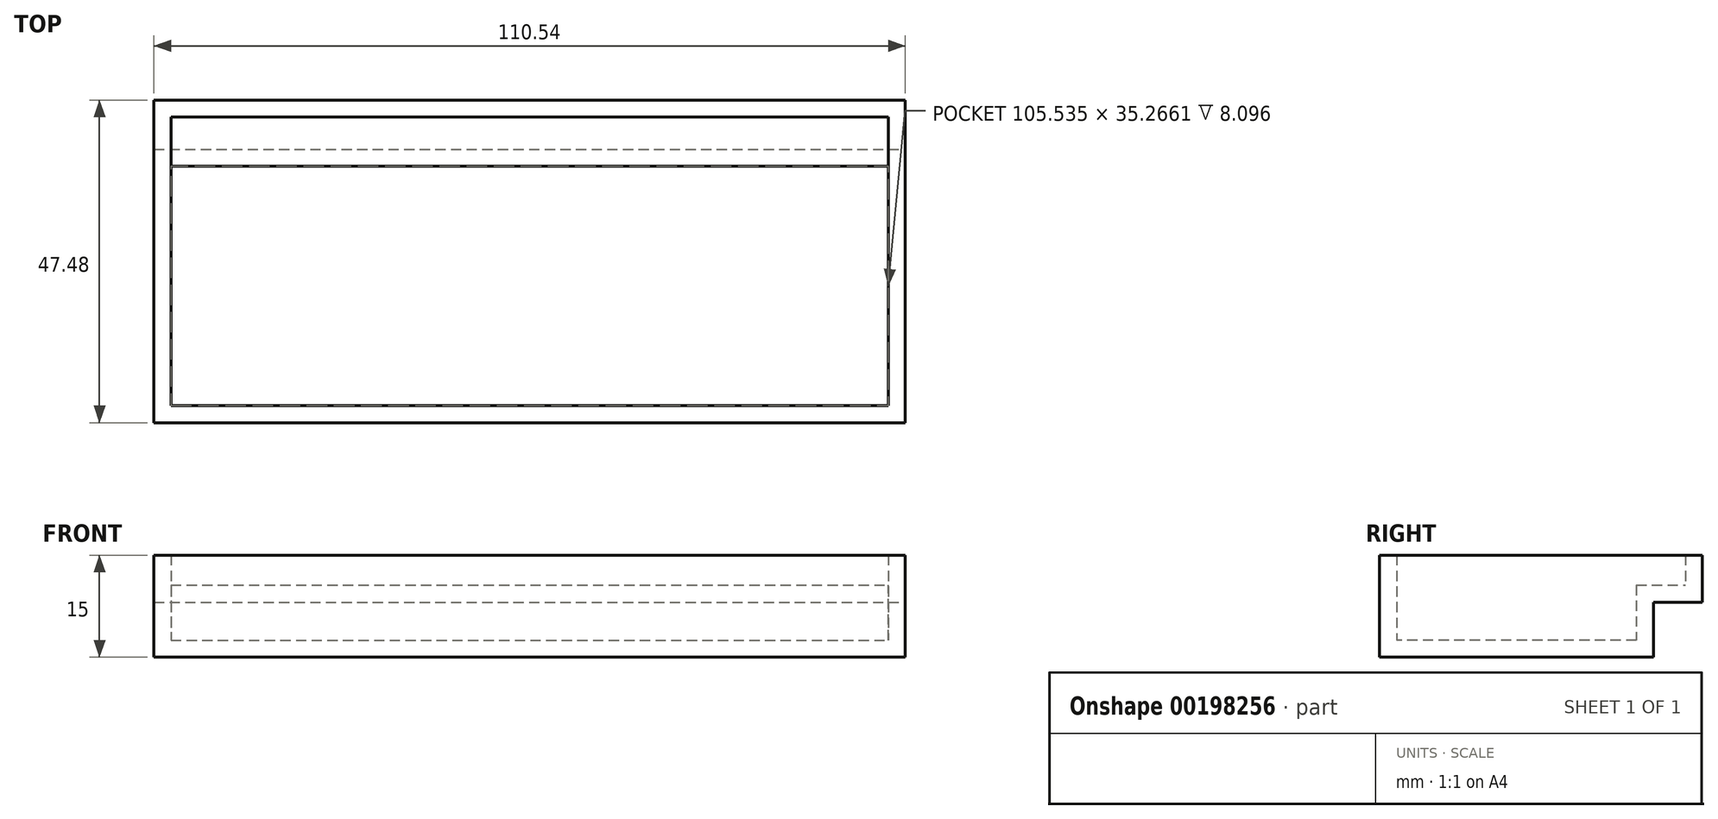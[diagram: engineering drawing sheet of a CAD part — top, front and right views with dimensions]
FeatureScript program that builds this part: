
annotation { "Feature Type Name" : "Feature", "Feature Type Description" : "" }
export const myFeature = defineFeature(function(context is Context, id is Id, definition is map)
    precondition{}
    {
        {
            var Q0;
            Q0=qCreatedBy(makeId("Top.planeOp"),FACE);
            var sketch = newSketch(context, id + "F0", { "sketchPlane" : qUnion([Q0])});
            skLineSegment(sketch, "E0.bottom", {"start": v(-55.88, 22.7) * mm, "end": v(54.66, 22.7) * mm});
            skLineSegment(sketch, "E0.top", {"start": v(-55.88, -24.79) * mm, "end": v(54.66, -24.79) * mm});
            skLineSegment(sketch, "E0.left", {"start": v(-55.88, 22.7) * mm, "end": v(-55.88, -24.79) * mm});
            skLineSegment(sketch, "E0.right", {"start": v(54.66, 22.7) * mm, "end": v(54.66, -24.79) * mm});
            skSolve(sketch);
        }
        {
            var Q0;
            Q0 = qSketchRegion(id + "F0", true);
            extrude(context, id + "F1", {"entities" : qUnion([Q0]), "depth" : 15 * mm});
        }
        {
            var Q0;
            Q0=makeQuery(id+"F1.opExtrude","SWEPT_FACE",FACE,{"disambiguationData":[OSD([sQuery(id+"F0.wireOp",EDGE,"E0.right")])]});
            var sketch = newSketch(context, id + "F2", { "sketchPlane" : qUnion([Q0])});
            skLineSegment(sketch, "E1.bottom", {"start": v(22.7, 0) * mm, "end": v(15.48, 0) * mm});
            skLineSegment(sketch, "E1.top", {"start": v(22.7, 8.1) * mm, "end": v(15.48, 8.1) * mm});
            skLineSegment(sketch, "E1.left", {"start": v(22.7, 0) * mm, "end": v(22.7, 8.1) * mm});
            skLineSegment(sketch, "E1.right", {"start": v(15.48, 0) * mm, "end": v(15.48, 8.1) * mm});
            skSolve(sketch);
        }
        {
            var Q0;
            Q0 = qSketchRegion(id + "F2", true);
            extrude(context, id + "F3", {"entities" : qUnion([Q0]), "operationType" : NewBodyOperationType.REMOVE, "endBound" : BoundingType.UP_TO_NEXT, "oppositeDirection" : true, "depth" : 25 * mm});
        }
        {
            var Q0;
            Q0=makeQuery(id+"F1.opExtrude","CAP_FACE",FACE,{"disambiguationData":[OSD([sQuery(id+"F0.wireOp",EDGE,"E0.bottom"),sQuery(id+"F0.wireOp",EDGE,"E0.top"),sQuery(id+"F0.wireOp",EDGE,"E0.left"),sQuery(id+"F0.wireOp",EDGE,"E0.right")])],"isStart":false});
            shell(context, id + "F4", {"entities" : qUnion([Q0]), "thickness" : 2.5 * mm});
        }
    });
